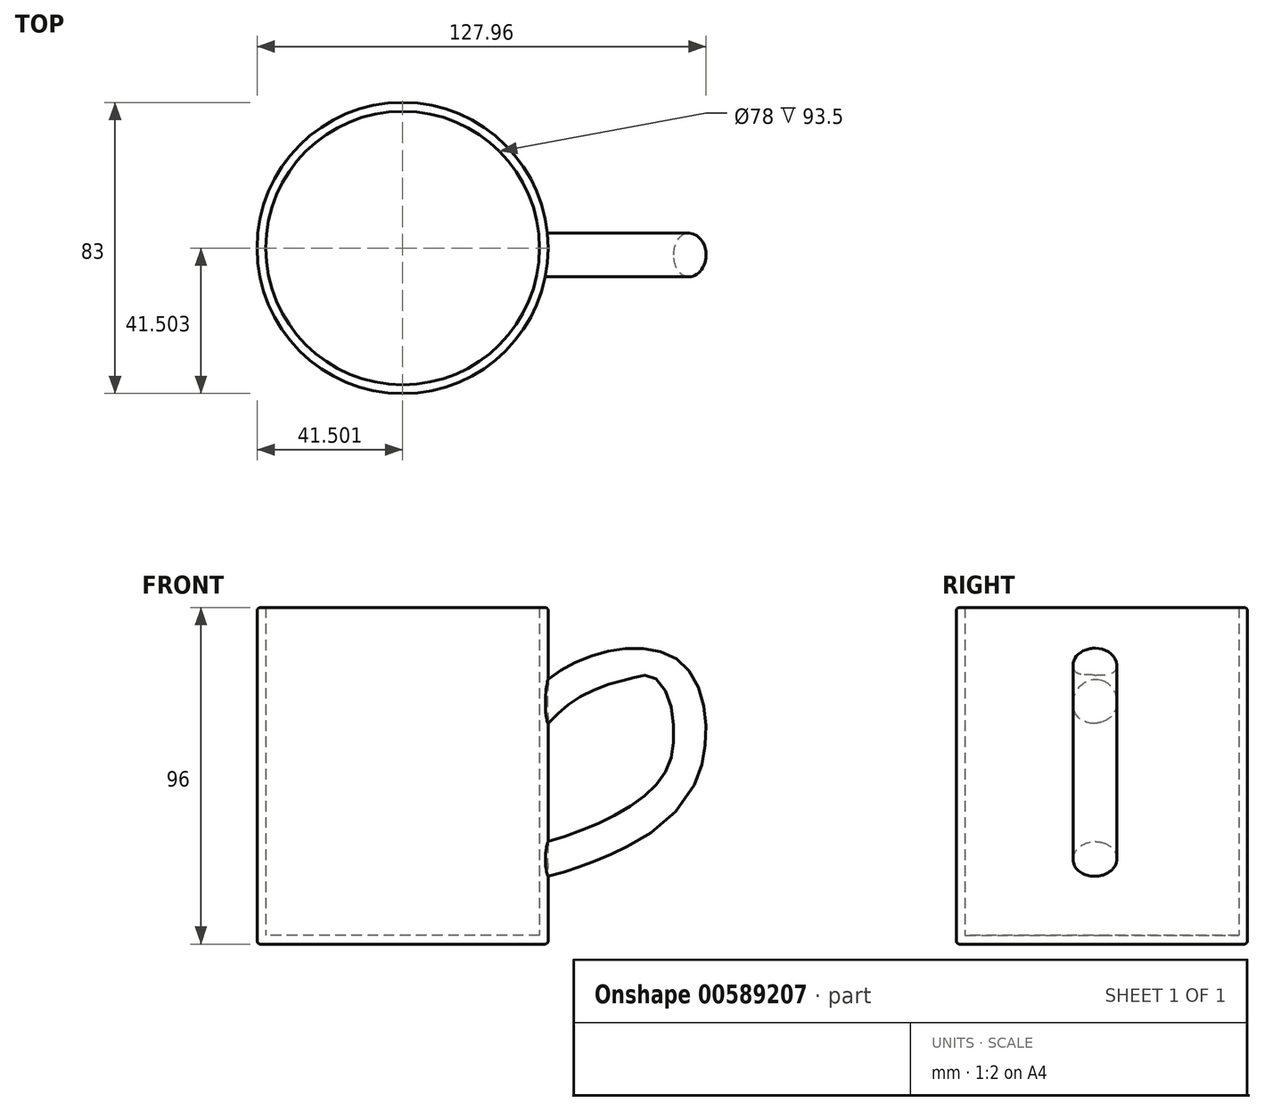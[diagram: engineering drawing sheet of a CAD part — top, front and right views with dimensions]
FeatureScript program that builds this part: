
annotation { "Feature Type Name" : "Feature", "Feature Type Description" : "" }
export const myFeature = defineFeature(function(context is Context, id is Id, definition is map)
    precondition{}
    {
        {
            var Q0;
            Q0=qCreatedBy(makeId("Top.planeOp"),FACE);
            var sketch = newSketch(context, id + "F0", { "sketchPlane" : qUnion([Q0])});
            skCircle(sketch, "E0", {"center": v(-5.17, 1.97) * mm, "radius": 41.5 * mm});
            skSolve(sketch);
        }
        {
            var Q0;
            Q0=makeQuery(id+"F0.imprint","IMPRINT",FACE,{"disambiguationData":[TD([[makeQuery(id+"F0.imprint","IMPRINT",EDGE,{"derivedFrom":sQuery(id+"F0.wireOp",EDGE,"E0")}),1.0]])]});
            extrude(context, id + "F1", {"entities" : qUnion([Q0]), "depth" : 96 * mm, "offsetDistance" : 25 * mm});
        }
        {
            var Q0;
            Q0=qCreatedBy(makeId("Right.planeOp"),FACE);
            cPlane(context, id + "F2", {"entities" : qUnion([Q0]), "cplaneType" : CPlaneType.OFFSET, "offset" : 36.5 * mm, "width" : 150 * mm, "height" : 150 * mm});
        }
        {
            var Q0;
            Q0=qCreatedBy(makeId("Front.planeOp"),FACE);
            var sketch = newSketch(context, id + "F3", { "sketchPlane" : qUnion([Q0])});
            skFitSpline(sketch, "E1", {"points": [v(33.64, 70.13) * mm, v(50.67, 80.24) * mm, v(73.17, 77.88) * mm, v(76.81, 48.96) * mm, v(57.53, 29.9) * mm, v(32, 20.8) * mm], "startDerivative": vector(77.05, 71.4) * mm, "endDerivative": vector(-121.8, -26.17) * mm});
            skSolve(sketch);
        }
        {
            var Q0;
            Q0=qCreatedBy(id+"F2.planeOp",FACE);
            var sketch = newSketch(context, id + "F4", { "sketchPlane" : qUnion([Q0])});
            skCircle(sketch, "E2", {"center": v(0, 69.44) * mm, "radius": 6.25 * mm});
            skCircle(sketch, "E3", {"center": v(0, 22.44) * mm, "radius": 6 * mm});
            skSolve(sketch);
        }
        {
            var Q0;
            Q0=makeQuery(id+"F4.imprint","IMPRINT",FACE,{"disambiguationData":[TD([[makeQuery(id+"F4.imprint","IMPRINT",EDGE,{"derivedFrom":sQuery(id+"F4.wireOp",EDGE,"E2")}),1.0]])]});
            var Q1;
            Q1=sQuery(id+"F3.wireOp",EDGE,"E1");
            sweep(context, id + "F5", {"operationType" : NewBodyOperationType.ADD, "profiles" : qUnion([Q0]), "path" : qUnion([Q1])});
        }
        {
            var Q0;
            Q0=makeQuery(id+"F1.opExtrude","CAP_FACE",FACE,{"disambiguationData":[OSD([sQuery(id+"F0.wireOp",EDGE,"E0")])],"isStart":false});
            shell(context, id + "F6", {"entities" : qUnion([Q0]), "thickness" : 2.5 * mm});
        }
        {
            var Q0;
            Q0=makeQuery(id+"F1.opExtrude","CAP_EDGE",EDGE,{"disambiguationData":[OSD([sQuery(id+"F0.wireOp",EDGE,"E0")])],"isStart":false});
            fillet(context, id + "F7", {"entities" : qUnion([Q0]), "radius" : 1 * mm, "tangentPropagation" : true, "allowEdgeOverflow" : false});
        }
        {
            var Q0;
            Q0=makeQuery(id+"F1.opExtrude","CAP_EDGE",EDGE,{"disambiguationData":[OSD([sQuery(id+"F0.wireOp",EDGE,"E0")])],"isStart":true});
            fillet(context, id + "F8", {"entities" : qUnion([Q0]), "radius" : 1 * mm, "tangentPropagation" : true, "allowEdgeOverflow" : false});
        }
    });
